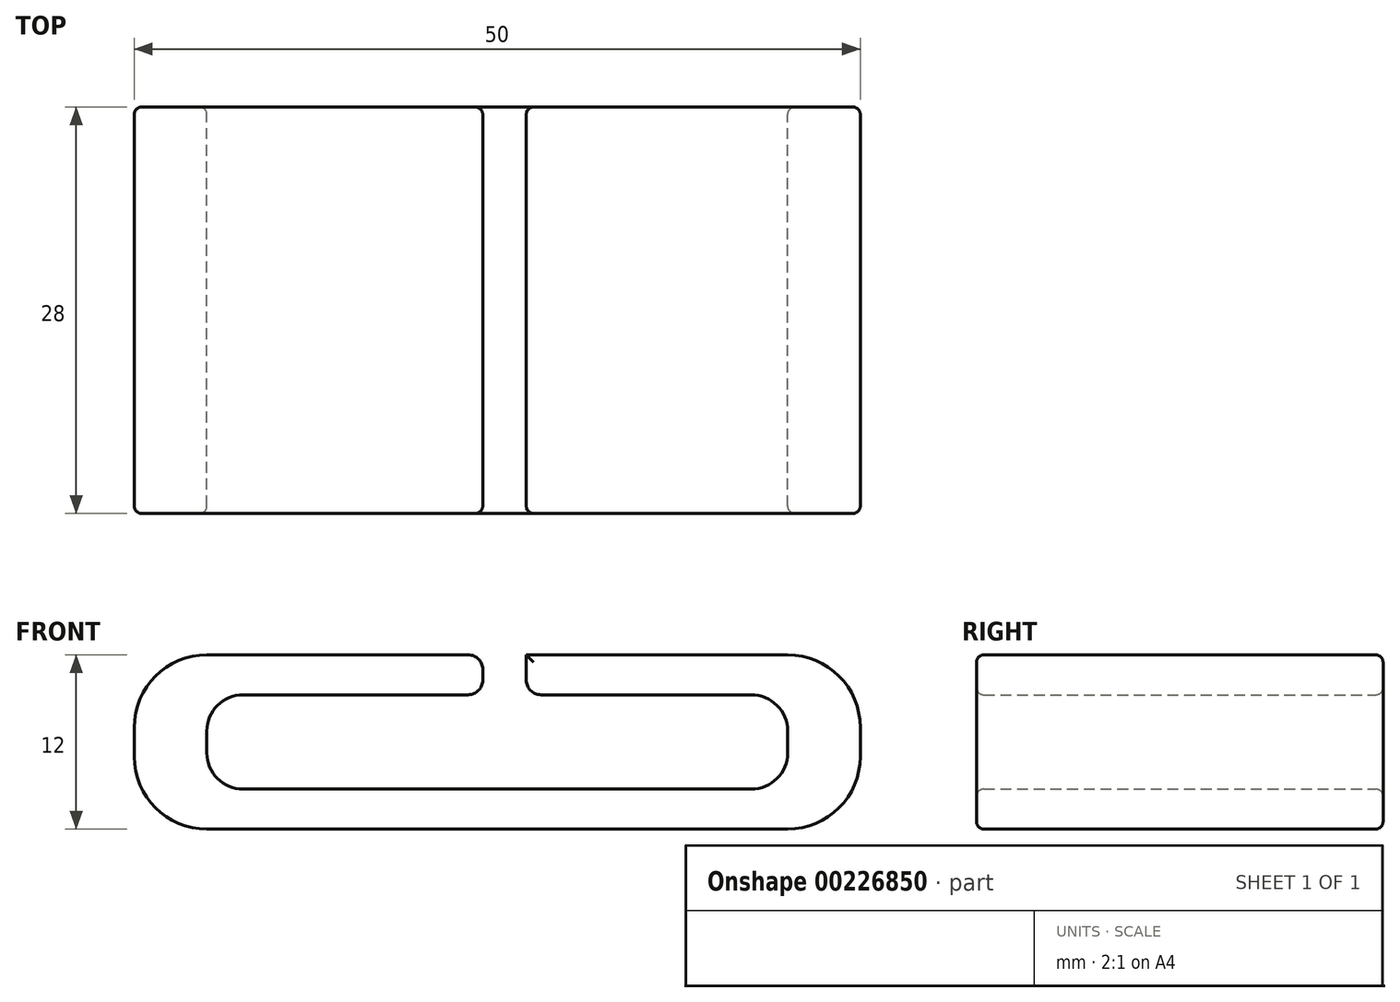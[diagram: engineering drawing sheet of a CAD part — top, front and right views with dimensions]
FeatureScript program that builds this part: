
annotation { "Feature Type Name" : "Feature", "Feature Type Description" : "" }
export const myFeature = defineFeature(function(context is Context, id is Id, definition is map)
    precondition{}
    {
        {
            var Q0;
            Q0=qCreatedBy(makeId("Top.planeOp"),FACE);
            var sketch = newSketch(context, id + "F0", { "sketchPlane" : qUnion([Q0])});
            skLineSegment(sketch, "E0.bottom", {"start": v(25, -14) * mm, "end": v(-25, -14) * mm});
            skLineSegment(sketch, "E0.top", {"start": v(25, 14) * mm, "end": v(-25, 14) * mm});
            skLineSegment(sketch, "E0.left", {"start": v(25, -14) * mm, "end": v(25, 14) * mm});
            skLineSegment(sketch, "E0.right", {"start": v(-25, -14) * mm, "end": v(-25, 14) * mm});
            skPoint(sketch, "E0.middle", {"position": v(0, 0) * mm});
            skSolve(sketch);
        }
        {
            var Q0;
            Q0 = qSketchRegion(id + "F0", true);
            extrude(context, id + "F1", {"entities" : qUnion([Q0]), "depth" : 12 * mm});
        }
        {
            var Q0;
            Q0=makeQuery(id+"F1.opExtrude","SWEPT_FACE",FACE,{"disambiguationData":[OSD([sQuery(id+"F0.wireOp",EDGE,"E0.top")])]});
            var sketch = newSketch(context, id + "F2", { "sketchPlane" : qUnion([Q0])});
            skLineSegment(sketch, "E1.bottom", {"start": v(-20, 9.25) * mm, "end": v(-2, 9.25) * mm});
            skLineSegment(sketch, "E1.top", {"start": v(-20, 2.75) * mm, "end": v(20, 2.75) * mm});
            skLineSegment(sketch, "E1.left", {"start": v(-20, 9.25) * mm, "end": v(-20, 2.75) * mm});
            skLineSegment(sketch, "E1.right", {"start": v(20, 9.25) * mm, "end": v(20, 2.75) * mm});
            skPoint(sketch, "E1.middle", {"position": v(0, 6) * mm});
            skPoint(sketch, "E1.middle.positionSnap0", {"position": v(25, 6) * mm});
            skPoint(sketch, "E1.middle.positionSnap1", {"position": v(0, 12) * mm});
            skPoint(sketch, "E1.centerSnap0", {"position": v(25, 6) * mm});
            skPoint(sketch, "E1.centerSnap1", {"position": v(0, 12) * mm});
            skLineSegment(sketch, "E2.bottom", {"start": v(-2, 12) * mm, "end": v(1, 12) * mm});
            skLineSegment(sketch, "E2.left", {"start": v(-2, 12) * mm, "end": v(-2, 9.25) * mm});
            skLineSegment(sketch, "E2.right", {"start": v(1, 12) * mm, "end": v(1, 9.25) * mm});
            skLineSegment(sketch, "E3.trimOffspring", {"start": v(1, 9.25) * mm, "end": v(20, 9.25) * mm});
            skSolve(sketch);
        }
        {
            var Q0;
            Q0 = qSketchRegion(id + "F2", true);
            extrude(context, id + "F3", {"entities" : qUnion([Q0]), "operationType" : NewBodyOperationType.REMOVE, "endBound" : BoundingType.THROUGH_ALL, "oppositeDirection" : true, "depth" : 25 * mm});
        }
        {
            var Q0;
            Q0=makeQuery(id+"F1.opExtrude","CAP_EDGE",EDGE,{"disambiguationData":[OSD([sQuery(id+"F0.wireOp",EDGE,"E0.left")])],"isStart":true});
            var Q1;
            Q1=makeQuery(id+"F1.opExtrude","CAP_EDGE",EDGE,{"disambiguationData":[OSD([sQuery(id+"F0.wireOp",EDGE,"E0.left")])],"isStart":false});
            var Q2;
            Q2=makeQuery(id+"F1.opExtrude","CAP_EDGE",EDGE,{"disambiguationData":[OSD([sQuery(id+"F0.wireOp",EDGE,"E0.right")])],"isStart":true});
            var Q3;
            Q3=makeQuery(id+"F1.opExtrude","CAP_EDGE",EDGE,{"disambiguationData":[OSD([sQuery(id+"F0.wireOp",EDGE,"E0.right")])],"isStart":false});
            fillet(context, id + "F4", {"entities" : qUnion([Q0, Q1, Q2, Q3]), "radius" : 5 * mm, "tangentPropagation" : true, "allowEdgeOverflow" : false});
        }
        {
            var Q0;
            Q0=makeQuery(id+"F3.boolean.opBoolean","COPY",EDGE,{"derivedFrom":makeQuery(id+"F3.opExtrude","SWEPT_EDGE",EDGE,{"disambiguationData":[OSD([sQuery(id+"F0.wireOp",EDGE,"E0.top"),sQuery(id+"F2.wireOp",EDGE,"E2.bottom"),sQuery(id+"F2.wireOp",EDGE,"E2.right")])]})});
            var Q1;
            Q1=makeQuery(id+"F3.boolean.opBoolean","COPY",EDGE,{"derivedFrom":makeQuery(id+"F3.opExtrude","SWEPT_EDGE",EDGE,{"disambiguationData":[OSD([sQuery(id+"F0.wireOp",EDGE,"E0.top"),sQuery(id+"F2.wireOp",EDGE,"E2.bottom"),sQuery(id+"F2.wireOp",EDGE,"E2.left")])]})});
            var Q2;
            Q2=makeQuery(id+"F3.boolean.opBoolean","COPY",EDGE,{"derivedFrom":makeQuery(id+"F3.opExtrude","SWEPT_EDGE",EDGE,{"disambiguationData":[OSD([sQuery(id+"F2.wireOp",EDGE,"E1.bottom"),sQuery(id+"F2.wireOp",EDGE,"E2.left")])]})});
            var Q3;
            Q3=makeQuery(id+"F3.boolean.opBoolean","COPY",EDGE,{"derivedFrom":makeQuery(id+"F3.opExtrude","SWEPT_EDGE",EDGE,{"disambiguationData":[OSD([sQuery(id+"F2.wireOp",EDGE,"E2.right"),sQuery(id+"F2.wireOp",EDGE,"E3.trimOffspring")])]})});
            fillet(context, id + "F5", {"entities" : qUnion([Q0, Q1, Q2, Q3]), "radius" : 1 * mm, "tangentPropagation" : true, "allowEdgeOverflow" : false});
        }
        {
            var Q0;
            Q0=makeQuery(id+"F3.boolean.opBoolean","COPY",EDGE,{"derivedFrom":makeQuery(id+"F3.opExtrude","SWEPT_EDGE",EDGE,{"disambiguationData":[OSD([sQuery(id+"F2.wireOp",EDGE,"E1.top"),sQuery(id+"F2.wireOp",EDGE,"E1.right")])]})});
            var Q1;
            Q1=makeQuery(id+"F3.boolean.opBoolean","COPY",EDGE,{"derivedFrom":makeQuery(id+"F3.opExtrude","SWEPT_EDGE",EDGE,{"disambiguationData":[OSD([sQuery(id+"F2.wireOp",EDGE,"E1.right"),sQuery(id+"F2.wireOp",EDGE,"E3.trimOffspring")])]})});
            var Q2;
            Q2=makeQuery(id+"F3.boolean.opBoolean","COPY",EDGE,{"derivedFrom":makeQuery(id+"F3.opExtrude","SWEPT_EDGE",EDGE,{"disambiguationData":[OSD([sQuery(id+"F2.wireOp",EDGE,"E1.bottom"),sQuery(id+"F2.wireOp",EDGE,"E1.left")])]})});
            var Q3;
            Q3=makeQuery(id+"F3.boolean.opBoolean","COPY",EDGE,{"derivedFrom":makeQuery(id+"F3.opExtrude","SWEPT_EDGE",EDGE,{"disambiguationData":[OSD([sQuery(id+"F2.wireOp",EDGE,"E1.top"),sQuery(id+"F2.wireOp",EDGE,"E1.left")])]})});
            fillet(context, id + "F6", {"entities" : qUnion([Q0, Q1, Q2, Q3]), "radius" : 2.5 * mm, "tangentPropagation" : true, "allowEdgeOverflow" : false});
        }
        {
            var Q0;
            Q0=makeQuery(id+"F1.opExtrude","SWEPT_FACE",FACE,{"disambiguationData":[OSD([sQuery(id+"F0.wireOp",EDGE,"E0.top")])]});
            var Q1;
            Q1=makeQuery(id+"F1.opExtrude","SWEPT_FACE",FACE,{"disambiguationData":[OSD([sQuery(id+"F0.wireOp",EDGE,"E0.bottom")])]});
            fillet(context, id + "F7", {"entities" : qUnion([Q0, Q1]), "radius" : .5 * mm, "tangentPropagation" : true, "allowEdgeOverflow" : false});
        }
    });
